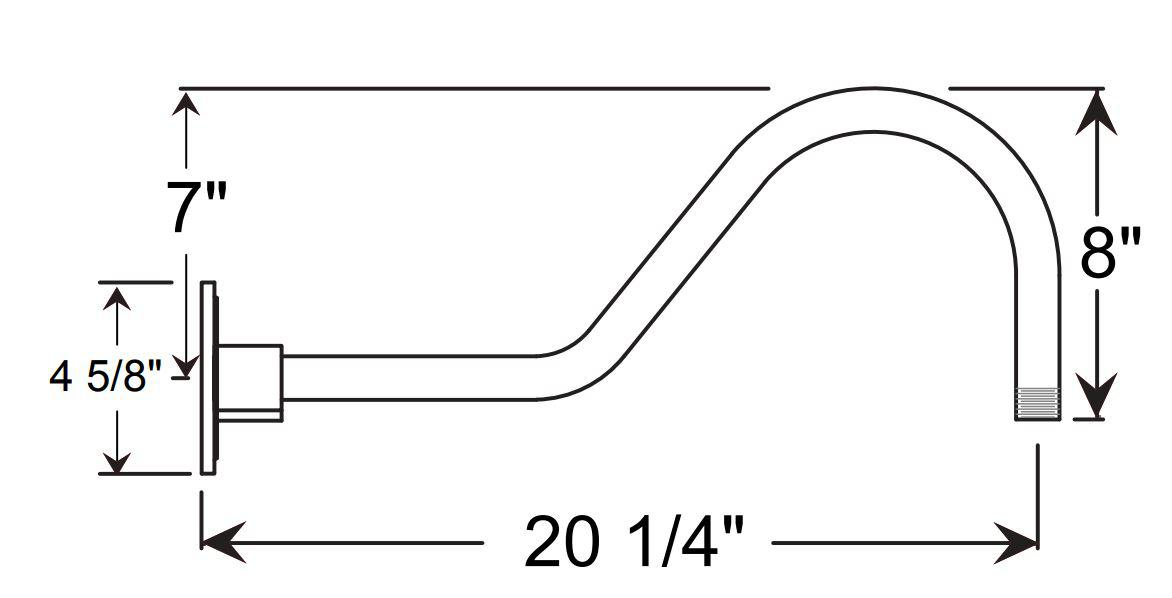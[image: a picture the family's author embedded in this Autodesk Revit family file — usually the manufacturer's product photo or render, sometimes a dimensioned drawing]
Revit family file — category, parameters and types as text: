
# Revit family: Warehouse LED 8,10,12,14,16,18,20,24,27
name_source: partatom
category: Lighting Fixtures
units: mm (PartAtom-declared; Revit-internal decimal feet)

## family parameters
Always vertical = Yes
Cut with Voids When Loaded = No
Light Source = Yes
OmniClass Number = 23.80.70.00
OmniClass Title = Lighting
Part Type = Normal
Room Calculation Point = No
Round Connector Dimension = Use Diameter
Shared = No
Work Plane-Based = No

## types (9) — shared parameters
BULB = Yes
Body Colour = Spun aluminium
Body Material = body
Bulb = Bulb
CRI = >90
Canopy Body = BLACK
Color Filter = 16777215
Construction Material = Heavy Duty spun aluminum.
Default Elevation = 0' - 0"
Description = 120-277 Voltage
Dimming = 1%
Dimming Lamp Color Temperature Shift = <None>
Efficiency = 65-125 lumens per watt
Lamp = LED
Life = L70 50,000 hours
Load Classification = Lighting
Manufacturer = ANP Lighting
Power Factor = 1
Tilt Angle = 90.00°
URL = https://www.anplighting.com
Voltage = 277 V
Warranty = 5 year limited warranty

## per-type parameters (varying)
| type | Apparent Load | Fixture Diameter | Fixture Height | Photometric Web File | W508 | W510 | W512 | W514 | W516 | W518 | W520 | W524 | W527 | Wattage Comments | Weight | a | b |
| W508 | 9 VA | 0' - 8" | 0' - 7" | W508M009LDNW40K.IES | Yes | No | No | No | No | No | No | No | No | 9 W | 1.0 lb | 0' - 7" | 0' - 2" |
| W510 | 10 VA | 0' - 10" | 0' - 6 1/2" | W510M010LDDW40K.IES | No | Yes | No | No | No | No | No | No | No | 10 W | 1.0 lb | 0' - 6 1/2" | 0' - 2" |
| W512 | 16 VA | 1' - 0 1/4" | 0' - 7 1/4" | W510M010LDDW40K.IES | No | No | Yes | No | No | No | No | No | No | 16 W | 1.0 lb | 0' - 7 1/4" | 0' - 2" |
| W514 | 16 VA | 1' - 2 3/4" | 0' - 7 1/4" | W514-100GLCL-32WPL-T15295-.ies | No | No | No | Yes | No | No | No | No | No | 16 W | 1.5 lbs | 0' - 7 1/4" | 0' - 2" |
| W516 | 16 VA | 1' - 4" | 0' - 8 3/4" | W516M016LDNW40K.IES | No | No | No | No | Yes | No | No | No | No | 16 W | 1.5 lbs | 0' - 8 3/4" | 0' - 2" |
| W518 | 24 VA | 1' - 6" | 0' - 9" | W518-100INC-T15300.IES | No | No | No | No | No | Yes | No | No | No | 24 W | 2.0 lbs | 0' - 9" | 0' - 2" |
| W520 | 24 VA | 1' - 8" | 0' - 10" | W520M024LDDW40K.IES | No | No | No | No | No | No | Yes | No | No | 24 W | 2.5 lbs | 0' - 10" | 0' - 2" |
| W524 | 37 VA | 2' - 0 1/4" | 1' - 3 1/2" | W520M024LDDW40K.IES | No | No | No | No | No | No | No | Yes | No | 37 W | 5.5 lbs | 1' - 3 1/2" | 0' - 3" |
| W527 | 37 VA | 2' - 3" | 1' - 4" | W527M037LDDW40K.IES | No | No | No | No | No | No | No | No | Yes | 37 W | 6.0 lbs | 1' - 4" | 0' - 3" |

note: column(s) folded — value = type name in every type: Model

## geometry (parser evidence)
native form markers: Sweep x47
no freeform markers — native parametric forms only
